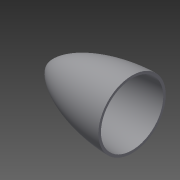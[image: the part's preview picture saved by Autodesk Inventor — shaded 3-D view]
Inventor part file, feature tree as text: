
AUTODESK INVENTOR PART (.ipt)
format: ipt  version: 2014 SP1 (Build 180222100, 222)  size: 202,240 bytes
history: native  units: mm
features: revolve x1, shell x1, sketch x1
ambient origin geometry x8: Origin, YZ Plane, XZ Plane, XY Plane, X Axis, Y Axis, Z Axis, Center Point
bodies: Solid1 (feature_tree)
feature tree (3):
  revolve  "Revolution1"  [1 undecoded]
  shell  "Shell1"  Thickness=90.0deg
  sketch  "Sketch1"  dims[d0=100.0mm d1=40.0mm d2=90.0deg d3=3.0mm]
note: 1 required parameter value undecoded (feature->parameter linkage not recoverable at this tier; creation-order binding heuristic only, values carry confidence <= 0.55)
